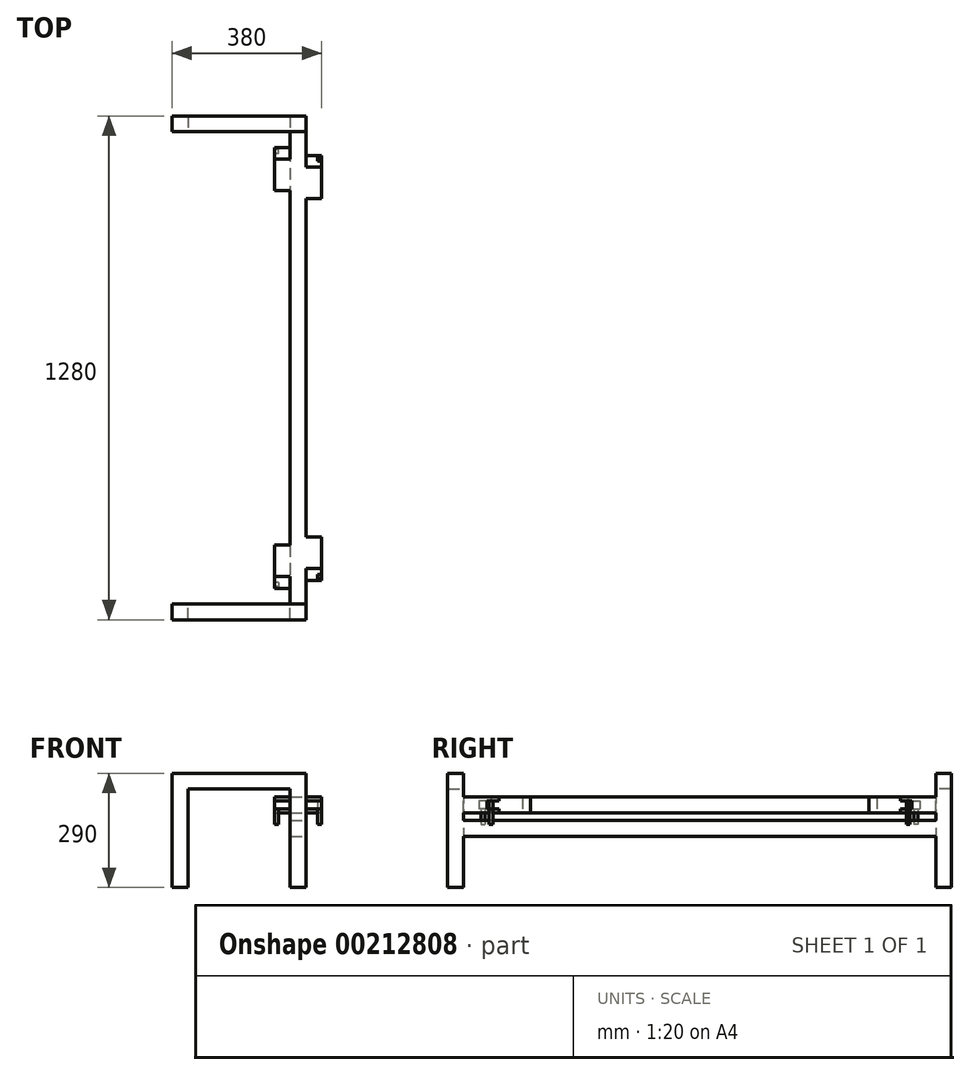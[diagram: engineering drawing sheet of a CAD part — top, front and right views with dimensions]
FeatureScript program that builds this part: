
annotation { "Feature Type Name" : "Feature", "Feature Type Description" : "" }
export const myFeature = defineFeature(function(context is Context, id is Id, definition is map)
    precondition{}
    {
        {
            var Q0;
            Q0=qCreatedBy(makeId("Front.planeOp"),FACE);
            var sketch = newSketch(context, id + "F0", { "sketchPlane" : qUnion([Q0])});
            skLineSegment(sketch, "E0.bottom", {"start": v(-170, 20) * mm, "end": v(170, 20) * mm});
            skLineSegment(sketch, "E0.top", {"start": v(-170, -20) * mm, "end": v(170, -20) * mm});
            skLineSegment(sketch, "E0.left", {"start": v(-170, 20) * mm, "end": v(-170, -20) * mm});
            skLineSegment(sketch, "E0.right", {"start": v(170, 20) * mm, "end": v(170, -20) * mm});
            skPoint(sketch, "E0.middle", {"position": v(0, 0) * mm});
            skLineSegment(sketch, "E1", {"start": v(-170, -20) * mm, "end": v(-170, -270) * mm});
            skLineSegment(sketch, "E2", {"start": v(-170, -270) * mm, "end": v(-130, -270) * mm});
            skLineSegment(sketch, "E3", {"start": v(-130, -270) * mm, "end": v(-130, -20) * mm});
            skLineSegment(sketch, "E4", {"start": v(170, -20) * mm, "end": v(170, -270) * mm});
            skLineSegment(sketch, "E5", {"start": v(170, -270) * mm, "end": v(130, -270) * mm});
            skLineSegment(sketch, "E6", {"start": v(130, -270) * mm, "end": v(130, -20) * mm});
            skLineSegment(sketch, "E7", {"start": v(-130, -270) * mm, "end": v(130, -270) * mm, "construction": true});
            skSolve(sketch);
        }
        {
            var Q0;
            Q0 = qSketchRegion(id + "F0", true);
            extrude(context, id + "F1", {"entities" : qUnion([Q0]), "depth" : 40 * mm});
        }
        {
            var Q0;
            Q0=makeQuery(id+"F1.opExtrude","CAP_FACE",FACE,{"disambiguationData":[OSD([sQuery(id+"F0.wireOp",EDGE,"E0.bottom"),sQuery(id+"F0.wireOp",EDGE,"E0.top"),sQuery(id+"F0.wireOp",EDGE,"E0.left"),sQuery(id+"F0.wireOp",EDGE,"E0.right"),sQuery(id+"F0.wireOp",EDGE,"E1"),sQuery(id+"F0.wireOp",EDGE,"E2"),sQuery(id+"F0.wireOp",EDGE,"E3"),sQuery(id+"F0.wireOp",EDGE,"E4"),sQuery(id+"F0.wireOp",EDGE,"E5"),sQuery(id+"F0.wireOp",EDGE,"E6")])],"isStart":true});
            var sketch = newSketch(context, id + "F2", { "sketchPlane" : qUnion([Q0])});
            skLineSegment(sketch, "E8.bottom", {"start": v(-130, -40) * mm, "end": v(-170, -40) * mm});
            skLineSegment(sketch, "E8.top", {"start": v(-130, -80) * mm, "end": v(-170, -80) * mm});
            skLineSegment(sketch, "E8.left", {"start": v(-130, -40) * mm, "end": v(-130, -80) * mm});
            skLineSegment(sketch, "E8.right", {"start": v(-170, -40) * mm, "end": v(-170, -80) * mm});
            skLineSegment(sketch, "E9.bottom", {"start": v(-130, -100) * mm, "end": v(-170, -100) * mm});
            skLineSegment(sketch, "E9.top", {"start": v(-130, -140) * mm, "end": v(-170, -140) * mm});
            skLineSegment(sketch, "E9.left", {"start": v(-130, -100) * mm, "end": v(-130, -140) * mm});
            skLineSegment(sketch, "E9.right", {"start": v(-170, -100) * mm, "end": v(-170, -140) * mm});
            skSolve(sketch);
        }
        {
            var Q0;
            Q0 = qSketchRegion(id + "F2", true);
            extrude(context, id + "F3", {"entities" : qUnion([Q0]), "operationType" : NewBodyOperationType.ADD, "depth" : 600 * mm});
        }
        {
            var Q0;
            Q0=makeQuery(id+"F3.boolean.opBoolean","MERGE",FACE,{"derivedFrom":[makeQuery(id+"F1.opExtrude","SWEPT_FACE",FACE,{"disambiguationData":[OSD([sQuery(id+"F0.wireOp",EDGE,"E0.right"),sQuery(id+"F0.wireOp",EDGE,"E4")])]}),makeQuery(id+"F3.opExtrude","SWEPT_FACE",FACE,{"disambiguationData":[OSD([sQuery(id+"F2.wireOp",EDGE,"E8.right")])]}),makeQuery(id+"F3.opExtrude","SWEPT_FACE",FACE,{"disambiguationData":[OSD([sQuery(id+"F2.wireOp",EDGE,"E9.right")])]})]});
            var sketch = newSketch(context, id + "F4", { "sketchPlane" : qUnion([Q0])});
            skLineSegment(sketch, "E10.bottom", {"start": v(170, -40) * mm, "end": v(90, -40) * mm});
            skLineSegment(sketch, "E10.top", {"start": v(170, -80) * mm, "end": v(90, -80) * mm});
            skLineSegment(sketch, "E10.left", {"start": v(170, -40) * mm, "end": v(170, -80) * mm});
            skLineSegment(sketch, "E10.right", {"start": v(90, -40) * mm, "end": v(90, -80) * mm});
            skLineSegment(sketch, "E11.bottom", {"start": v(90, -70) * mm, "end": v(60, -70) * mm});
            skLineSegment(sketch, "E11.top", {"start": v(90, -50) * mm, "end": v(60, -50) * mm});
            skLineSegment(sketch, "E11.left", {"start": v(90, -70) * mm, "end": v(90, -50) * mm});
            skLineSegment(sketch, "E11.right", {"start": v(60, -70) * mm, "end": v(60, -50) * mm});
            skSolve(sketch);
        }
        {
            var Q0;
            Q0 = qSketchRegion(id + "F4", true);
            extrude(context, id + "F5", {"entities" : qUnion([Q0]), "depth" : 40 * mm});
        }
        {
            var Q0;
            Q0=makeQuery(id+"F5.opExtrude","CAP_FACE",FACE,{"disambiguationData":[OSD([sQuery(id+"F4.wireOp",EDGE,"E10.bottom"),sQuery(id+"F4.wireOp",EDGE,"E10.top"),sQuery(id+"F4.wireOp",EDGE,"E10.left"),sQuery(id+"F4.wireOp",EDGE,"E10.right"),sQuery(id+"F4.wireOp",EDGE,"rBqocDEy-4knL-I3Kj-cL0q-fr6crbfK2529.top"),sQuery(id+"F4.wireOp",EDGE,"rBqocDEy-4knL-I3Kj-cL0q-fr6crbfK2529.left"),sQuery(id+"F4.wireOp",EDGE,"rBqocDEy-4knL-I3Kj-cL0q-fr6crbfK2529.right")])],"isStart":false});
            var sketch = newSketch(context, id + "F6", { "sketchPlane" : qUnion([Q0])});
            skLineSegment(sketch, "E12.bottom", {"start": v(75, -50) * mm, "end": v(65, -50) * mm});
            skLineSegment(sketch, "E12.top", {"start": v(75, -110) * mm, "end": v(65, -110) * mm});
            skLineSegment(sketch, "E12.left", {"start": v(75, -50) * mm, "end": v(75, -110) * mm});
            skLineSegment(sketch, "E12.right", {"start": v(65, -50) * mm, "end": v(65, -110) * mm});
            skSolve(sketch);
        }
        {
            var Q0;
            Q0 = qSketchRegion(id + "F6", true);
            extrude(context, id + "F7", {"entities" : qUnion([Q0]), "oppositeDirection" : true, "depth" : 10 * mm});
        }
        {
            var Q0;
            Q0=makeQuery(id+"F3.boolean.opBoolean","MERGE",FACE,{"derivedFrom":[makeQuery(id+"F1.opExtrude","SWEPT_FACE",FACE,{"disambiguationData":[OSD([sQuery(id+"F0.wireOp",EDGE,"E6")])]}),makeQuery(id+"F3.opExtrude","SWEPT_FACE",FACE,{"disambiguationData":[OSD([sQuery(id+"F2.wireOp",EDGE,"E8.left")])]}),makeQuery(id+"F3.opExtrude","SWEPT_FACE",FACE,{"disambiguationData":[OSD([sQuery(id+"F2.wireOp",EDGE,"E9.left")])]})]});
            var sketch = newSketch(context, id + "F8", { "sketchPlane" : qUnion([Q0])});
            skLineSegment(sketch, "E13.bottom", {"start": v(-150, -40) * mm, "end": v(-70, -40) * mm});
            skLineSegment(sketch, "E13.top", {"start": v(-150, -80) * mm, "end": v(-70, -80) * mm});
            skLineSegment(sketch, "E13.left", {"start": v(-150, -40) * mm, "end": v(-150, -80) * mm});
            skLineSegment(sketch, "E13.right", {"start": v(-70, -40) * mm, "end": v(-70, -80) * mm});
            skLineSegment(sketch, "E14.bottom", {"start": v(-70, -50) * mm, "end": v(-40, -50) * mm});
            skLineSegment(sketch, "E14.top", {"start": v(-70, -70) * mm, "end": v(-40, -70) * mm});
            skLineSegment(sketch, "E14.left", {"start": v(-70, -50) * mm, "end": v(-70, -70) * mm});
            skLineSegment(sketch, "E14.right", {"start": v(-40, -50) * mm, "end": v(-40, -70) * mm});
            skSolve(sketch);
        }
        {
            var Q0;
            Q0 = qSketchRegion(id + "F8", true);
            extrude(context, id + "F9", {"entities" : qUnion([Q0]), "depth" : 40 * mm});
        }
        {
            var Q0;
            Q0=makeQuery(id+"F9.opExtrude","CAP_FACE",FACE,{"disambiguationData":[OSD([sQuery(id+"F8.wireOp",EDGE,"E13.bottom"),sQuery(id+"F8.wireOp",EDGE,"E13.top"),sQuery(id+"F8.wireOp",EDGE,"E13.left"),sQuery(id+"F8.wireOp",EDGE,"E13.right"),sQuery(id+"F8.wireOp",EDGE,"E14.bottom"),sQuery(id+"F8.wireOp",EDGE,"E14.top"),sQuery(id+"F8.wireOp",EDGE,"E14.right")])],"isStart":false});
            var sketch = newSketch(context, id + "F10", { "sketchPlane" : qUnion([Q0])});
            skLineSegment(sketch, "E15.bottom", {"start": v(-45, -50) * mm, "end": v(-55, -50) * mm});
            skLineSegment(sketch, "E15.top", {"start": v(-45, -110) * mm, "end": v(-55, -110) * mm});
            skLineSegment(sketch, "E15.left", {"start": v(-45, -50) * mm, "end": v(-45, -110) * mm});
            skLineSegment(sketch, "E15.right", {"start": v(-55, -50) * mm, "end": v(-55, -110) * mm});
            skSolve(sketch);
        }
        {
            var Q0;
            Q0 = qSketchRegion(id + "F10", true);
            extrude(context, id + "F11", {"entities" : qUnion([Q0]), "operationType" : NewBodyOperationType.ADD, "oppositeDirection" : true, "depth" : 10 * mm});
        }
        {
            var Q0;
            Q0=makeQuery(id+"F5.opExtrude","SWEPT_BODY",BODY,{"disambiguationData":[OSD([sQuery(id+"F4.wireOp",EDGE,"E10.bottom"),sQuery(id+"F4.wireOp",EDGE,"E10.top"),sQuery(id+"F4.wireOp",EDGE,"E10.left"),sQuery(id+"F4.wireOp",EDGE,"E10.right"),sQuery(id+"F4.wireOp",EDGE,"E11.bottom"),sQuery(id+"F4.wireOp",EDGE,"E11.top"),sQuery(id+"F4.wireOp",EDGE,"E11.right")])]});
            var Q1;
            Q1=makeQuery(id+"F7.opExtrude","SWEPT_BODY",BODY,{"disambiguationData":[OSD([sQuery(id+"F6.wireOp",EDGE,"E12.bottom"),sQuery(id+"F6.wireOp",EDGE,"E12.top"),sQuery(id+"F6.wireOp",EDGE,"E12.left"),sQuery(id+"F6.wireOp",EDGE,"E12.right")])]});
            var Q2;
            Q2=makeQuery(id+"F9.opExtrude","SWEPT_BODY",BODY,{"disambiguationData":[OSD([sQuery(id+"F8.wireOp",EDGE,"E13.bottom"),sQuery(id+"F8.wireOp",EDGE,"E13.top"),sQuery(id+"F8.wireOp",EDGE,"E13.left"),sQuery(id+"F8.wireOp",EDGE,"E13.right"),sQuery(id+"F8.wireOp",EDGE,"E14.bottom"),sQuery(id+"F8.wireOp",EDGE,"E14.top"),sQuery(id+"F8.wireOp",EDGE,"E14.right")])]});
            var Q3;
            Q3=makeQuery(id+"F11.opExtrude","SWEPT_BODY",BODY,{"disambiguationData":[OSD([sQuery(id+"F10.wireOp",EDGE,"E15.bottom"),sQuery(id+"F10.wireOp",EDGE,"E15.top"),sQuery(id+"F10.wireOp",EDGE,"E15.left"),sQuery(id+"F10.wireOp",EDGE,"E15.right")])]});
            var Q4;
            Q4=makeQuery(id+"F3.opExtrude","CAP_FACE",FACE,{"disambiguationData":[OSD([sQuery(id+"F2.wireOp",EDGE,"E8.bottom"),sQuery(id+"F2.wireOp",EDGE,"E8.top"),sQuery(id+"F2.wireOp",EDGE,"E8.left"),sQuery(id+"F2.wireOp",EDGE,"E8.right")])],"isStart":false});
            mirror(context, id + "F12", {"entities" : qUnion([Q0, Q1, Q2, Q3]), "mirrorPlane" : qUnion([Q4])});
        }
        {
            var Q0;
            Q0=makeQuery(id+"F1.opExtrude","SWEPT_BODY",BODY,{"disambiguationData":[OSD([sQuery(id+"F0.wireOp",EDGE,"E0.bottom"),sQuery(id+"F0.wireOp",EDGE,"E0.top"),sQuery(id+"F0.wireOp",EDGE,"E0.left"),sQuery(id+"F0.wireOp",EDGE,"E0.right"),sQuery(id+"F0.wireOp",EDGE,"E1"),sQuery(id+"F0.wireOp",EDGE,"E2"),sQuery(id+"F0.wireOp",EDGE,"E3"),sQuery(id+"F0.wireOp",EDGE,"E4"),sQuery(id+"F0.wireOp",EDGE,"E5"),sQuery(id+"F0.wireOp",EDGE,"E6")])]});
            var Q1;
            Q1=makeQuery(id+"F3.opExtrude","CAP_FACE",FACE,{"disambiguationData":[OSD([sQuery(id+"F2.wireOp",EDGE,"E8.bottom"),sQuery(id+"F2.wireOp",EDGE,"E8.top"),sQuery(id+"F2.wireOp",EDGE,"E8.left"),sQuery(id+"F2.wireOp",EDGE,"E8.right")])],"isStart":false});
            mirror(context, id + "F13", {"operationType" : NewBodyOperationType.ADD, "entities" : qUnion([Q0]), "mirrorPlane" : qUnion([Q1])});
        }
    });
